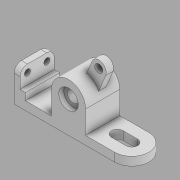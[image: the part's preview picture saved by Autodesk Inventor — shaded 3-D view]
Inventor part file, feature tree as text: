
AUTODESK INVENTOR PART (.ipt)
format: ipt  version: 2020 (Build 240168000, 168)  size: 250,368 bytes
history: native  units: in
note: dims shown in document units (in); Inventor stores cm internally (conversion verified against a paired STEP export)
features: sketch x10, extrude x9, other x2, projected_geometry x2, hole x1
ambient origin geometry x8: Origin, YZ Plane, XZ Plane, XY Plane, X Axis, Y Axis, Z Axis, Center Point
bodies: Body1 (feature_tree), Body2 (feature_tree)
feature tree (24):
  other  "Sólido1"
  extrude  "Base"  Depth=1.75in
  extrude  "RedondeoIzquierda"  Depth=0.81in
  extrude  "RedondeoDerecha"  Depth=0.44in
  extrude  "HuecoDerecha"  Depth=1.62in
  hole  "AgujeroCentral"  [1 undecoded]
  extrude  "HuecosIzquierda"  Depth=0.31in TaperAngle=0.0deg
  extrude  "Protuberancia"  Depth=1.76in
  extrude  "RestoFrontalProtuberancia"  Depth=0.88in
  extrude  "RestoTraseroProtuberancia"  Depth=1.76in
  extrude  "HuecoProtuberancia"  Depth=0.594in
  sketch  "Boceto1"  dims[d0=0.31in d1=1.75in]
  sketch  "Boceto2"  dims[d2=0.28in d3=0.81in]
  sketch  "Boceto3"  dims[d4=5.48in d5=0.44in]
  sketch  "Boceto4"  dims[d6=2.5in d7=1.62in]
  sketch  "Boceto5"  dims[d8=1.76in d9=1.76in d10=0.0in]
  sketch  "Boceto6"  dims[d11=0.38in d12=0.31in d13=0.0in]
  sketch  "Boceto7"  dims[d14=0.88in d15=1.76in]
  projected_geometry  "Contorno proyectado1"
  projected_geometry  "Contorno proyectado2"
  other  "Sólido2"
  sketch  "Boceto8"  dims[d16=0.88in d17=2.81in]
  sketch  "Boceto9"  dims[d18=2.38in d19=1.76in]
  sketch  "Boceto10"  dims[d20=0.44in d21=0.0in d22=0.594in d23=1.76in d24=0.583in d26=0.75in d27=0.44in d28=0.0in d29=0.609in d30=0.75in d31=1.0in d32=0.25in d33=0.5635in d34=1.0in d35=0.8108in d36=0.312in d37=0.312in d38=0.38in d39=0.38in d40=0.38in d41=0.38in d42=1.37in d43=1.0in d44=0.31in d45=0.0in d48=0.88in d49=1.62in d50=60.0deg d51=0.76in d52=1.76in d53=0.0in d54=0.75in d55=0.0in d56=0.63in d57=0.0in d58=0.406in d59=0.38in d60=0.0in]
note: 1 required parameter value undecoded (feature->parameter linkage not recoverable at this tier; creation-order binding heuristic only, values carry confidence <= 0.55)
